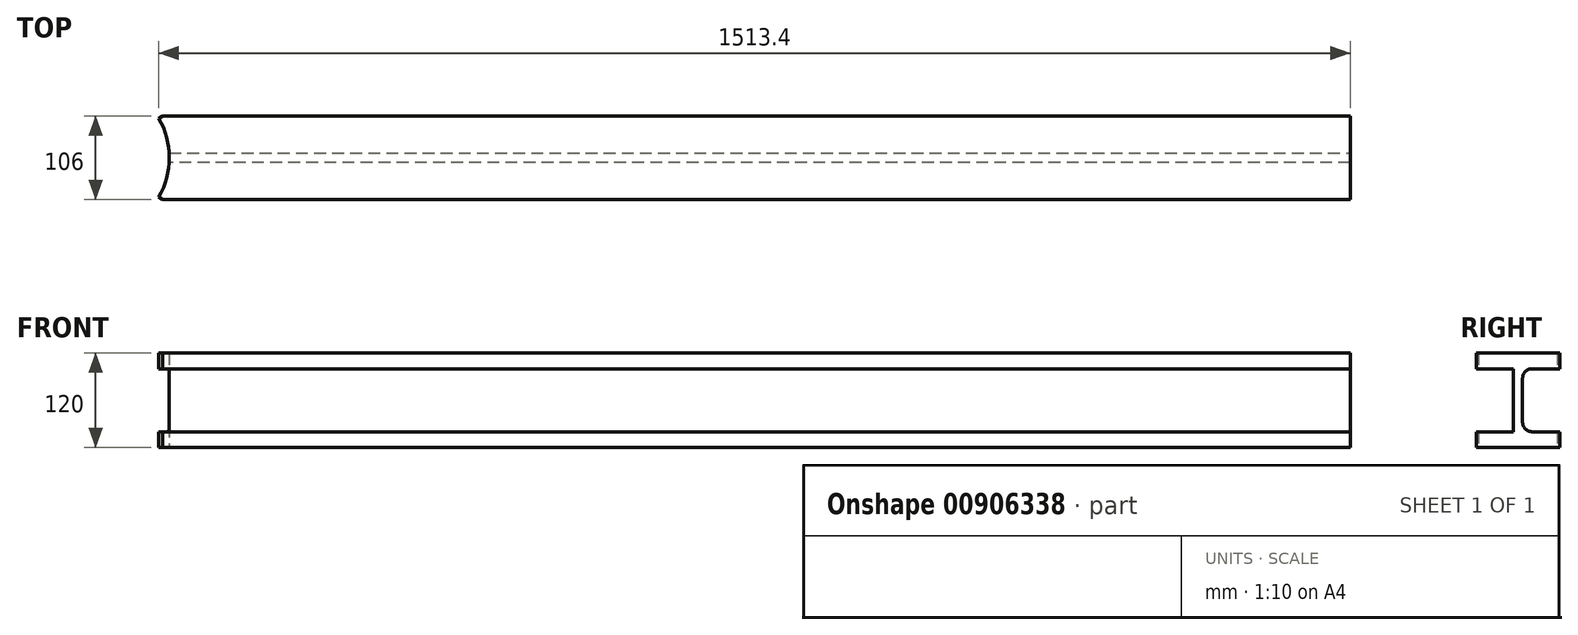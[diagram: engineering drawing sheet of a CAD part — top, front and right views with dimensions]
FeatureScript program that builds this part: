
annotation { "Feature Type Name" : "Feature", "Feature Type Description" : "" }
export const myFeature = defineFeature(function(context is Context, id is Id, definition is map)
    precondition{}
    {
        {
            var Q0;
            Q0=qCreatedBy(makeId("Top.planeOp"),FACE);
            var sketch = newSketch(context, id + "F0", { "sketchPlane" : qUnion([Q0])});
            skArc(sketch, "E0", {"start": v(86.6, -50) * mm, "mid": v(100, 0) * mm, "end": v(86.6, 50) * mm, "construction": true});
            skLineSegment(sketch, "E1", {"start": v(0, 0) * mm, "end": v(1600, 0) * mm, "construction": true});
            skLineSegment(sketch, "E2", {"start": v(1600, 0) * mm, "end": v(1600, -53) * mm});
            skLineSegment(sketch, "E3", {"start": v(1600, -53) * mm, "end": v(91.8, -53) * mm});
            skLineSegment(sketch, "E4.MirrorCS", {"start": v(1600, 0) * mm, "end": v(1600, 53) * mm});
            skLineSegment(sketch, "E5.MirrorCS", {"start": v(1600, 53) * mm, "end": v(91.8, 53) * mm});
            skLineSegment(sketch, "E6.MirrorCS", {"start": v(845.9, 1359.15) * mm, "end": v(91.8, 53) * mm, "construction": true});
            skLineSegment(sketch, "E7.MirrorCS", {"start": v(0, 0) * mm, "end": v(800, 1385.64) * mm, "construction": true});
            skLineSegment(sketch, "E8", {"start": v(91.8, 53) * mm, "end": v(86.6, 50) * mm});
            skLineSegment(sketch, "E9.MirrorCS", {"start": v(91.8, -53) * mm, "end": v(86.6, -50) * mm});
            skLineSegment(sketch, "E10", {"start": v(0, 0) * mm, "end": v(86.6, 50) * mm, "construction": true});
            skArc(sketch, "E11", {"start": v(86.6, -50) * mm, "mid": v(100, 0) * mm, "end": v(86.6, 50) * mm});
            skPoint(sketch, "E12.orphan", {"position": v(84.8, -53) * mm});
            skPoint(sketch, "E13.orphan", {"position": v(84.8, 53) * mm});
            skSolve(sketch);
        }
        {
            var Q0;
            Q0=makeQuery(id+"F0.imprint","IMPRINT",FACE,{"disambiguationData":[TD([[makeQuery(id+"F0.imprint","IMPRINT",EDGE,{"derivedFrom":sQuery(id+"F0.wireOp",EDGE,"E2")}),-1.0]])]});
            extrude(context, id + "F1", {"entities" : qUnion([Q0]), "depth" : 20 * mm, "offsetDistance" : 25 * mm});
        }
        {
            var Q0;
            Q0=makeQuery(id+"F1.opExtrude","CAP_FACE",FACE,{"disambiguationData":[OSD([sQuery(id+"F0.wireOp",EDGE,"E2"),sQuery(id+"F0.wireOp",EDGE,"E3"),sQuery(id+"F0.wireOp",EDGE,"E4.MirrorCS"),sQuery(id+"F0.wireOp",EDGE,"E5.MirrorCS"),sQuery(id+"F0.wireOp",EDGE,"E8"),sQuery(id+"F0.wireOp",EDGE,"E9.MirrorCS"),sQuery(id+"F0.wireOp",EDGE,"E11")])],"isStart":false});
            var sketch = newSketch(context, id + "F2", { "sketchPlane" : qUnion([Q0])});
            skArc(sketch, "E14", {"start": v(99.82, -6) * mm, "mid": v(100, 0) * mm, "end": v(99.82, 6) * mm});
            skLineSegment(sketch, "E15", {"start": v(99.82, 6) * mm, "end": v(1600, 6) * mm});
            skLineSegment(sketch, "E16", {"start": v(1600, 6) * mm, "end": v(1600, -6) * mm});
            skLineSegment(sketch, "E17", {"start": v(1600, -6) * mm, "end": v(99.82, -6) * mm});
            skSolve(sketch);
        }
        {
            var Q0;
            Q0 = qSketchRegion(id + "F2", true);
            extrude(context, id + "F3", {"entities" : qUnion([Q0]), "operationType" : NewBodyOperationType.ADD, "depth" : 80 * mm, "offsetDistance" : 25 * mm});
        }
        {
            var Q0;
            Q0=makeQuery(id+"F3.opExtrude","CAP_FACE",FACE,{"disambiguationData":[OSD([sQuery(id+"F2.wireOp",EDGE,"E14"),sQuery(id+"F2.wireOp",EDGE,"E15"),sQuery(id+"F2.wireOp",EDGE,"E16"),sQuery(id+"F2.wireOp",EDGE,"E17")])],"isStart":false});
            var sketch = newSketch(context, id + "F4", { "sketchPlane" : qUnion([Q0])});
            skArc(sketch, "E18", {"start": v(86.6, -50) * mm, "mid": v(100, 0) * mm, "end": v(86.6, 50) * mm});
            skLineSegment(sketch, "E19.bottom", {"start": v(91.8, -53) * mm, "end": v(1600, -53) * mm});
            skLineSegment(sketch, "E19.top", {"start": v(91.8, 53) * mm, "end": v(1600, 53) * mm});
            skLineSegment(sketch, "E19.right", {"start": v(1600, -53) * mm, "end": v(1600, 53) * mm});
            skLineSegment(sketch, "E20", {"start": v(86.6, 50) * mm, "end": v(91.8, 53) * mm});
            skLineSegment(sketch, "E21.MirrorCS", {"start": v(86.6, -50) * mm, "end": v(91.8, -53) * mm});
            skPoint(sketch, "E22.orphan", {"position": v(98.82, 57.05) * mm});
            skPoint(sketch, "E23.orphan", {"position": v(84.8, 53) * mm});
            skPoint(sketch, "E24.orphan", {"position": v(84.8, 48.96) * mm});
            skPoint(sketch, "E25.orphan", {"position": v(98.82, -57.05) * mm});
            skPoint(sketch, "E26.orphan", {"position": v(84.8, -48.96) * mm});
            skSolve(sketch);
        }
        {
            var Q0;
            Q0 = qSketchRegion(id + "F4", true);
            extrude(context, id + "F5", {"entities" : qUnion([Q0]), "operationType" : NewBodyOperationType.ADD, "depth" : 20 * mm, "offsetDistance" : 25 * mm});
        }
        {
            var Q0;
            Q0=makeQuery(id+"F3.opExtrude","CAP_EDGE",EDGE,{"disambiguationData":[OSD([sQuery(id+"F2.wireOp",EDGE,"E15")])],"isStart":true});
            var Q1;
            Q1=makeQuery(id+"F3.opExtrude","CAP_EDGE",EDGE,{"disambiguationData":[OSD([sQuery(id+"F2.wireOp",EDGE,"E17")])],"isStart":true});
            var Q2;
            Q2=makeQuery(id+"F3.opExtrude","CAP_EDGE",EDGE,{"disambiguationData":[OSD([sQuery(id+"F2.wireOp",EDGE,"E15")])],"isStart":false});
            var Q3;
            Q3=makeQuery(id+"F3.opExtrude","CAP_EDGE",EDGE,{"disambiguationData":[OSD([sQuery(id+"F2.wireOp",EDGE,"E17")])],"isStart":false});
            fillet(context, id + "F6", {"entities" : qUnion([Q0, Q1, Q2, Q3]), "radius" : 12 * mm, "tangentPropagation" : true, "allowEdgeOverflow" : false});
        }
    });
